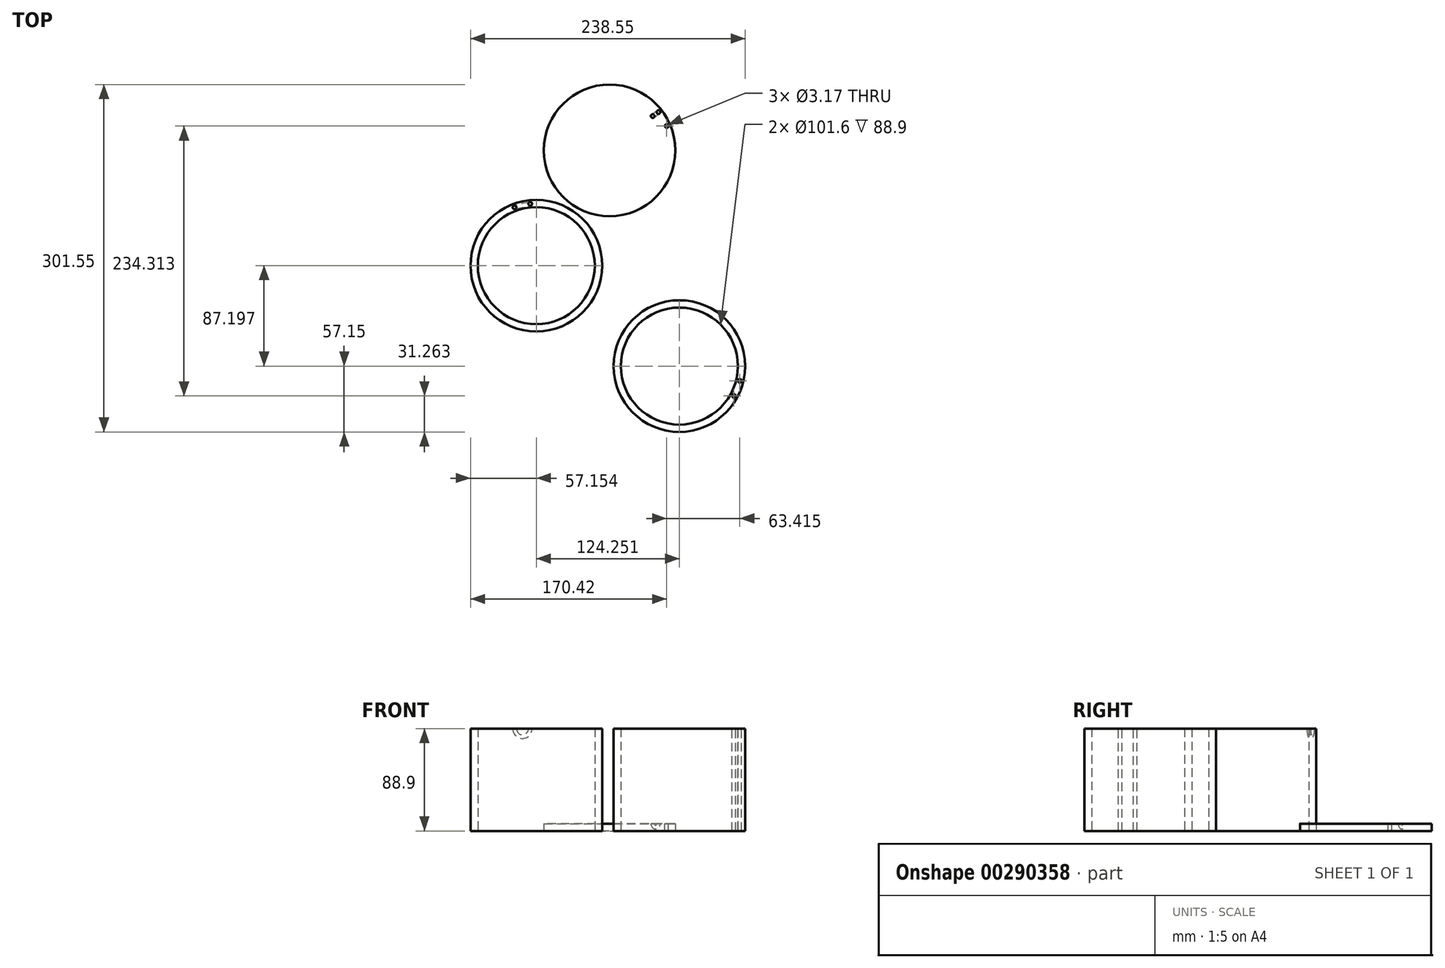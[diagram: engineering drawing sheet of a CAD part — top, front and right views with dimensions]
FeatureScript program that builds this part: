
annotation { "Feature Type Name" : "Feature", "Feature Type Description" : "" }
export const myFeature = defineFeature(function(context is Context, id is Id, definition is map)
    precondition{}
    {
        {
            var Q0;
            Q0=qCreatedBy(makeId("Top.planeOp"),FACE);
            var sketch = newSketch(context, id + "F0", { "sketchPlane" : qUnion([Q0])});
            skCircle(sketch, "E0", {"center": v(-5.37, 19.87) * mm, "radius": 57.15 * mm});
            skCircle(sketch, "E1", {"center": v(-5.37, 19.87) * mm, "radius": 50.8 * mm});
            skSolve(sketch);
        }
        {
            var Q0;
            Q0=makeQuery(id+"F0.imprint","IMPRINT",FACE,{"disambiguationData":[TD([[makeQuery(id+"F0.imprint","IMPRINT",EDGE,{"derivedFrom":sQuery(id+"F0.wireOp",EDGE,"E0")}),1.0]])]});
            extrude(context, id + "F1", {"entities" : qUnion([Q0]), "depth" : 88.9 * mm});
        }
        {
            var Q0;
            Q0=makeQuery(id+"F1.opExtrude","CAP_FACE",FACE,{"disambiguationData":[OSD([sQuery(id+"F0.wireOp",EDGE,"E0"),sQuery(id+"F0.wireOp",EDGE,"E1")])],"isStart":true});
            var sketch = newSketch(context, id + "F2", { "sketchPlane" : qUnion([Q0])});
            skCircle(sketch, "E2", {"center": v(-5.37, -19.87) * mm, "radius": 57.15 * mm});
            skPoint(sketch, "E2.first.point", {"position": v(-50.42, -55.02) * mm});
            skPoint(sketch, "E2.second.point", {"position": v(33.56, 21.97) * mm});
            skPoint(sketch, "E2.third.point", {"position": v(32.93, -62.3) * mm});
            skSolve(sketch);
        }
        {
            var Q0;
            Q0=makeQuery(id+"F1.opExtrude","CAP_FACE",FACE,{"disambiguationData":[OSD([sQuery(id+"F0.wireOp",EDGE,"E0"),sQuery(id+"F0.wireOp",EDGE,"E1")])],"isStart":false});
            var sketch = newSketch(context, id + "F3", { "sketchPlane" : qUnion([Q0])});
            skPoint(sketch, "E3", {"position": v(42, -6.02) * mm});
            skLineSegment(sketch, "E4", {"start": v(42, 1.5) * mm, "end": v(47.92, -0.8) * mm, "construction": true});
            skPoint(sketch, "E5.MirrorP", {"position": v(47.06, 7.05) * mm});
            skSolve(sketch);
        }
        {
            var Q0;
            Q0=sQuery(id+"F3.wireOp",VERTEX,"E3");
            var Q1;
            Q1=makeQuery(id+"F1.opExtrude","SWEPT_BODY",BODY,{"disambiguationData":[OSD([sQuery(id+"F0.wireOp",EDGE,"E0"),sQuery(id+"F0.wireOp",EDGE,"E1")])]});
            hole(context, id + "F4", {"style" : HoleStyle.SIMPLE, "endStyle" : HoleEndStyle.THROUGH, "holeDiameter" : 3.17 * mm, "tappedDepth" : 12.7 * mm, "tapClearance" : 3, "locations" : qUnion([Q0]), "scope" : qUnion([Q1])});
        }
        {
            var Q0;
            Q0=qCreatedBy(makeId("Top.planeOp"),FACE);
            var sketch = newSketch(context, id + "F5", { "sketchPlane" : qUnion([Q0])});
            skCircle(sketch, "E6", {"center": v(-201.93, 9.77) * mm, "radius": 57.15 * mm});
            skSolve(sketch);
        }
        {
            var Q0;
            Q0=makeQuery(id+"F5.imprint","IMPRINT",FACE,{"disambiguationData":[TD([[makeQuery(id+"F5.imprint","IMPRINT",EDGE,{"derivedFrom":sQuery(id+"F5.wireOp",EDGE,"E6")}),1.0]])]});
            extrude(context, id + "F6", {"entities" : qUnion([Q0]), "depth" : 6.35 * mm});
        }
        {
            var Q0;
            Q0=makeQuery(id+"F6.opExtrude","CAP_FACE",FACE,{"disambiguationData":[OSD([sQuery(id+"F5.wireOp",EDGE,"E6")])],"isStart":false});
            var sketch = newSketch(context, id + "F7", { "sketchPlane" : qUnion([Q0])});
            skCircle(sketch, "E7", {"center": v(-201.93, 9.77) * mm, "radius": 50.8 * mm, "construction": true});
            skPoint(sketch, "E8", {"position": v(-223.03, 59.44) * mm});
            skCircle(sketch, "E9", {"center": v(-223.03, 59.44) * mm, "radius": 1.59 * mm});
            skLineSegment(sketch, "E10", {"start": v(-243.42, 49.07) * mm, "end": v(-194, 66.36) * mm, "construction": true});
            skSolve(sketch);
        }
        {
            var Q0;
            Q0=makeQuery(id+"F7.imprint","IMPRINT",FACE,{"disambiguationData":[TD([[makeQuery(id+"F7.imprint","IMPRINT",EDGE,{"derivedFrom":sQuery(id+"F7.wireOp",EDGE,"E9")}),1.0]])]});
            var Q1;
            Q1=sQuery(id+"F7.wireOp",EDGE,"E9");
            var Q2;
            Q2=sQuery(id+"F7.wireOp",EDGE,"E10");
            revolve(context, id + "F8", {"operationType" : NewBodyOperationType.REMOVE, "entities" : qUnion([Q0]), "surfaceEntities" : qUnion([Q1]), "axis" : qUnion([Q2]), "revolveType" : RevolveType.ONE_DIRECTION, "oppositeDirection" : true, "angle" : 180 * degree});
        }
        {
            var Q0;
            Q0=sQuery(id+"F3.wireOp",VERTEX,"E5.MirrorP");
            var Q1;
            Q1=makeQuery(id+"F1.opExtrude","SWEPT_BODY",BODY,{"disambiguationData":[OSD([sQuery(id+"F0.wireOp",EDGE,"E0"),sQuery(id+"F0.wireOp",EDGE,"E1")])]});
            hole(context, id + "F9", {"style" : HoleStyle.SIMPLE, "endStyle" : HoleEndStyle.THROUGH, "holeDiameter" : 3.17 * mm, "tappedDepth" : 12.7 * mm, "tapClearance" : 3, "locations" : qUnion([Q0]), "scope" : qUnion([Q1])});
        }
        {
            var Q0;
            Q0=makeQuery(id+"F6.opExtrude","CAP_FACE",FACE,{"disambiguationData":[OSD([sQuery(id+"F5.wireOp",EDGE,"E6")])],"isStart":false});
            var sketch = newSketch(context, id + "F10", { "sketchPlane" : qUnion([Q0])});
            skCircle(sketch, "E11", {"center": v(-223.03, 59.44) * mm, "radius": 14.02 * mm});
            skPoint(sketch, "E12", {"position": v(-209.53, 63.2) * mm});
            skSolve(sketch);
        }
        {
            var Q0;
            Q0=sQuery(id+"F10.wireOp",VERTEX,"E12");
            var Q1;
            Q1=makeQuery(id+"F6.opExtrude","SWEPT_BODY",BODY,{"disambiguationData":[OSD([sQuery(id+"F5.wireOp",EDGE,"E6")])]});
            hole(context, id + "F11", {"style" : HoleStyle.SIMPLE, "endStyle" : HoleEndStyle.THROUGH, "holeDiameter" : 3.17 * mm, "tappedDepth" : 12.7 * mm, "tapClearance" : 3, "locations" : qUnion([Q0]), "scope" : qUnion([Q1])});
        }
        {
            var Q0;
            Q0=qCreatedBy(makeId("Top.planeOp"),FACE);
            var sketch = newSketch(context, id + "F12", { "sketchPlane" : qUnion([Q0])});
            skCircle(sketch, "E13", {"center": v(-129.62, 107.07) * mm, "radius": 57.15 * mm});
            skCircle(sketch, "E14", {"center": v(-129.62, 107.07) * mm, "radius": 50.8 * mm});
            skSolve(sketch);
        }
        {
            var Q0;
            Q0=makeQuery(id+"F12.imprint","IMPRINT",FACE,{"disambiguationData":[TD([[makeQuery(id+"F12.imprint","IMPRINT",EDGE,{"derivedFrom":sQuery(id+"F12.wireOp",EDGE,"E13")}),1.0]])]});
            extrude(context, id + "F13", {"entities" : qUnion([Q0]), "depth" : 88.9 * mm});
        }
        {
            var Q0;
            Q0=makeQuery(id+"F13.opExtrude","CAP_FACE",FACE,{"disambiguationData":[OSD([sQuery(id+"F12.wireOp",EDGE,"E13"),sQuery(id+"F12.wireOp",EDGE,"E14")])],"isStart":false});
            var sketch = newSketch(context, id + "F14", { "sketchPlane" : qUnion([Q0])});
            skPoint(sketch, "E15", {"position": v(-134.84, 160.79) * mm});
            skLineSegment(sketch, "E16", {"start": v(-142.48, 162.75) * mm, "end": v(-141.05, 156.56) * mm, "construction": true});
            skCircle(sketch, "E17", {"center": v(-134.84, 160.79) * mm, "radius": 1.59 * mm});
            skSolve(sketch);
        }
        {
            var Q0;
            Q0=makeQuery(id+"F14.imprint","IMPRINT",FACE,{"disambiguationData":[TD([[makeQuery(id+"F14.imprint","IMPRINT",EDGE,{"derivedFrom":sQuery(id+"F14.wireOp",EDGE,"E17")}),1.0]])]});
            var Q1;
            Q1=sQuery(id+"F14.wireOp",EDGE,"E16");
            revolve(context, id + "F15", {"operationType" : NewBodyOperationType.REMOVE, "entities" : qUnion([Q0]), "axis" : qUnion([Q1]), "revolveType" : RevolveType.ONE_DIRECTION, "oppositeDirection" : true, "angle" : 180 * degree});
        }
        {
            var Q0;
            Q0=makeQuery(id+"F6.opExtrude","SWEPT_BODY",BODY,{"disambiguationData":[OSD([sQuery(id+"F5.wireOp",EDGE,"E6")])]});
            var Q1;
            Q1=sQuery(id+"F2.wireOp",EDGE,"E2");
            transform(context, id + "F16", {"entities" : qUnion([Q0]), "transformType" : TransformType.ROTATION, "transformAxis" : qUnion([Q1]), "angle" : 75 * degree, "makeCopy" : false});
        }
    });
